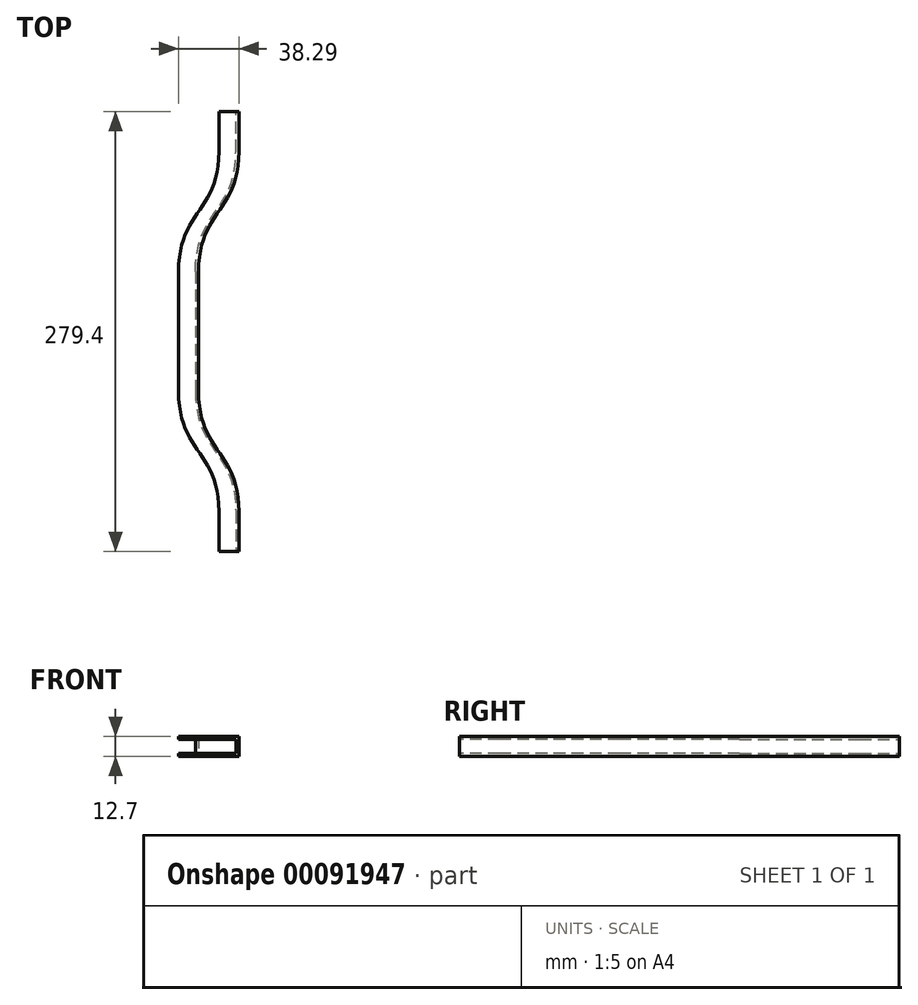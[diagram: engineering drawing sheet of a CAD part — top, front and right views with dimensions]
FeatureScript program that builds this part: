
annotation { "Feature Type Name" : "Feature", "Feature Type Description" : "" }
export const myFeature = defineFeature(function(context is Context, id is Id, definition is map)
    precondition{}
    {
        {
            var Q0;
            Q0=qCreatedBy(makeId("Top.planeOp"),FACE);
            var sketch = newSketch(context, id + "F0", { "sketchPlane" : qUnion([Q0])});
            skLineSegment(sketch, "E0", {"start": v(0, -38.1) * mm, "end": v(0, 0) * mm});
            skFitSpline(sketch, "E1", {"points": [v(0, -38.1) * mm, v(12.7, -76.2) * mm, v(25.6, -114.3) * mm], "startDerivative": vector(0, -114.34) * mm, "endDerivative": vector(0, -114.26) * mm});
            skLineSegment(sketch, "E2", {"start": v(12.7, -96.94) * mm, "end": v(12.7, -55.46) * mm, "construction": true});
            skLineSegment(sketch, "E3", {"start": v(25.6, -114.3) * mm, "end": v(25.6, -139.7) * mm});
            skSolve(sketch);
        }
        {
            var Q0;
            Q0=qCreatedBy(makeId("Front.planeOp"),FACE);
            var sketch = newSketch(context, id + "F1", { "sketchPlane" : qUnion([Q0])});
            skLineSegment(sketch, "E4.bottom", {"start": v(6.35, 6.35) * mm, "end": v(-6.35, 6.35) * mm});
            skLineSegment(sketch, "E4.top", {"start": v(6.35, -6.35) * mm, "end": v(-6.35, -6.35) * mm});
            skLineSegment(sketch, "E4.left", {"start": v(6.35, 6.35) * mm, "end": v(6.35, -6.35) * mm});
            skPoint(sketch, "E4.middle", {"position": v(0, 0) * mm});
            skLineSegment(sketch, "E5.0", {"start": v(4.45, -4.45) * mm, "end": v(-6.35, -4.45) * mm});
            skLineSegment(sketch, "E5.1", {"start": v(4.44, 4.45) * mm, "end": v(4.45, -4.45) * mm});
            skLineSegment(sketch, "E5.2", {"start": v(4.44, 4.45) * mm, "end": v(-6.35, 4.45) * mm});
            skLineSegment(sketch, "E6", {"start": v(-6.35, -6.35) * mm, "end": v(-6.35, -4.45) * mm});
            skLineSegment(sketch, "E7", {"start": v(-6.35, 4.45) * mm, "end": v(-6.35, 6.35) * mm});
            skSolve(sketch);
        }
        {
            var Q0;
            Q0 = qSketchRegion(id + "F1", true);
            var Q1;
            Q1 = qConstructionFilter(qBodyType(qCreatedBy(id + "F1" ,EDGE), BodyType.WIRE), ConstructionObject.NO);
            var Q2;
            Q2 = qConstructionFilter(qBodyType(qCreatedBy(id + "F0" ,EDGE), BodyType.WIRE), ConstructionObject.NO);
            sweep(context, id + "F2", {"profiles" : qUnion([Q0]), "surfaceProfiles" : qUnion([Q1]), "path" : qUnion([Q2]), "keepProfileOrientation" : true});
        }
        {
            var Q0;
            Q0=makeQuery(id+"F2.opSweep","SWEPT_BODY",BODY,{"disambiguationData":[OSD([sQuery(id+"F0.wireOp",EDGE,"E3"),sQuery(id+"F1.wireOp",EDGE,"E7")])]});
            var Q1;
            Q1=qCreatedBy(makeId("Front.planeOp"),FACE);
            mirror(context, id + "F3", {"operationType" : NewBodyOperationType.ADD, "entities" : qUnion([Q0]), "mirrorPlane" : qUnion([Q1])});
        }
    });
